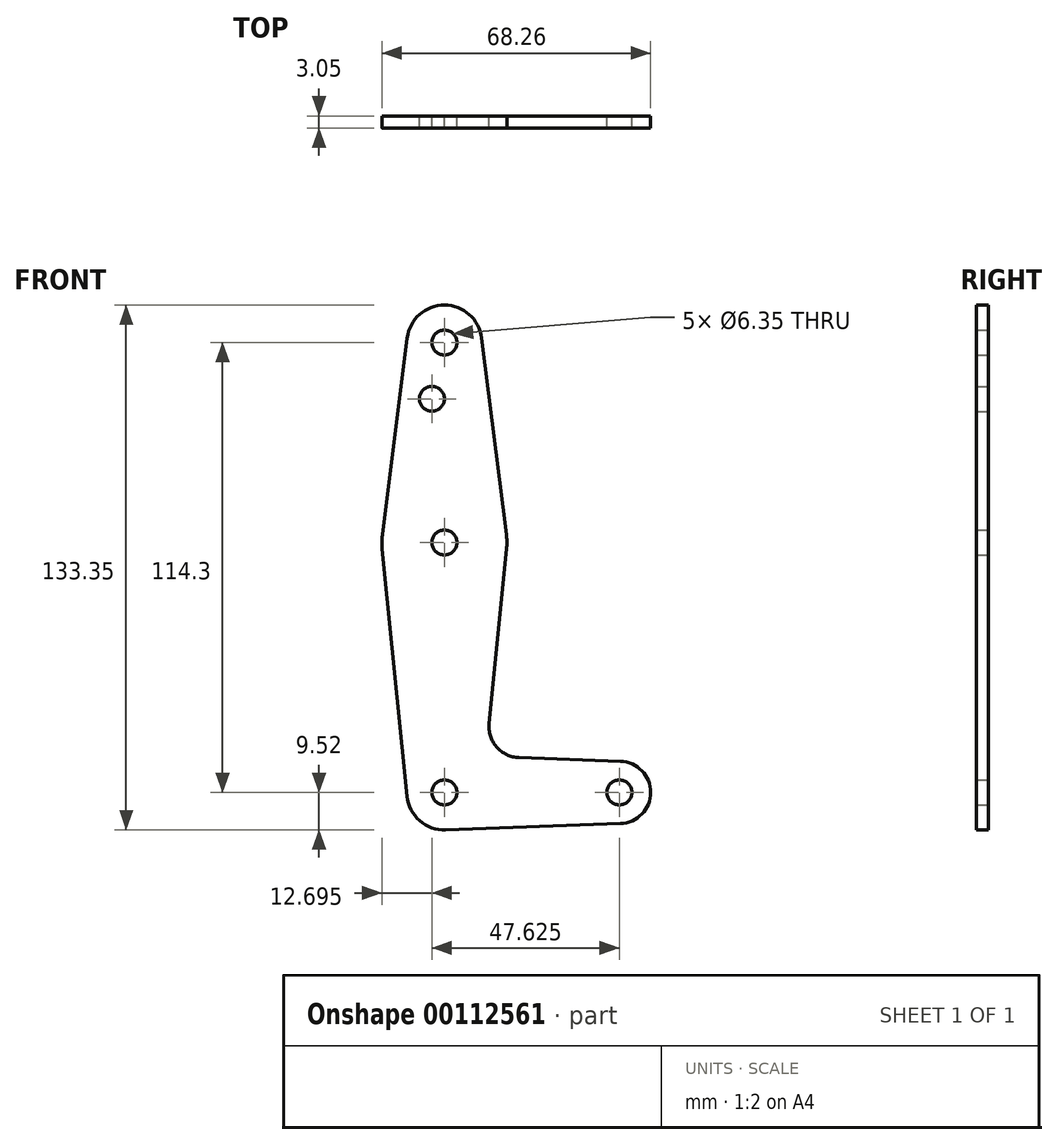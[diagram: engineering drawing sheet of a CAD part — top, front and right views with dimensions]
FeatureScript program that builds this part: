
annotation { "Feature Type Name" : "Feature", "Feature Type Description" : "" }
export const myFeature = defineFeature(function(context is Context, id is Id, definition is map)
    precondition{}
    {
        {
            var Q0;
            Q0=qCreatedBy(makeId("Front.planeOp"),FACE);
            var sketch = newSketch(context, id + "F0", { "sketchPlane" : qUnion([Q0])});
            skLineSegment(sketch, "E0", {"start": v(0, 0) * mm, "end": v(0, 114.3) * mm});
            skLineSegment(sketch, "E1", {"start": v(0, 0) * mm, "end": v(44.45, 0) * mm});
            skCircle(sketch, "E2", {"center": v(0, 114.3) * mm, "radius": 9.53 * mm});
            skCircle(sketch, "E3", {"center": v(0, 0) * mm, "radius": 9.53 * mm});
            skCircle(sketch, "E4", {"center": v(44.45, 0) * mm, "radius": 7.94 * mm});
            skCircle(sketch, "E5", {"center": v(0, 63.5) * mm, "radius": 15.88 * mm});
            skLineSegment(sketch, "E6", {"start": v(-9.45, 115.5) * mm, "end": v(-15.75, 65.48) * mm});
            skLineSegment(sketch, "E7", {"start": v(9.45, 115.5) * mm, "end": v(15.75, 65.48) * mm});
            skLineSegment(sketch, "E8", {"start": v(-15.8, 61.91) * mm, "end": v(-9.48, -0.95) * mm});
            skLineSegment(sketch, "E9", {"start": v(15.8, 61.91) * mm, "end": v(11.34, 17.58) * mm});
            skLineSegment(sketch, "E10", {"start": v(18.95, 8.85) * mm, "end": v(44.73, 7.93) * mm});
            skLineSegment(sketch, "E11", {"start": v(0.34, -9.52) * mm, "end": v(44.73, -7.93) * mm});
            skCircle(sketch, "E12", {"center": v(0, 114.3) * mm, "radius": 3.18 * mm});
            skCircle(sketch, "E13", {"center": v(0, 63.5) * mm, "radius": 3.18 * mm});
            skCircle(sketch, "E14", {"center": v(0, 0) * mm, "radius": 3.18 * mm});
            skCircle(sketch, "E15", {"center": v(44.45, 0) * mm, "radius": 3.18 * mm});
            skCircle(sketch, "E16", {"center": v(-3.18, 100.01) * mm, "radius": 3.18 * mm});
            skArc(sketch, "E17.filletArc", {"start": v(11.34, 17.58) * mm, "mid": v(13.26, 11.57) * mm, "end": v(18.95, 8.85) * mm});
            skSolve(sketch);
        }
        {
            var Q0;
            Q0 = qSketchRegion(id + "F0", true);
            var Q1;
            {var subQ0=sQuery(id+"F0.wireOp",EDGE,"E14");var subQ1=sQuery(id+"F0.wireOp",EDGE,"E0");var subQ2=makeQuery(id+"F0.imprint","INTERSECT",VERTEX,{"derivedFrom":[subQ1,subQ0]});Q1=makeQuery(id+"F0.imprint","IMPRINT",FACE,{"disambiguationData":[TD([[makeQuery(id+"F0.imprint","IMPRINT",EDGE,{"disambiguationData":[TD([[subQ2,-1.0]])],"derivedFrom":subQ1}),-1.0]])]});}
            extrude(context, id + "F1", {"entities" : qUnion([Q0, Q1]), "depth" : 3.05 * mm});
        }
    });
